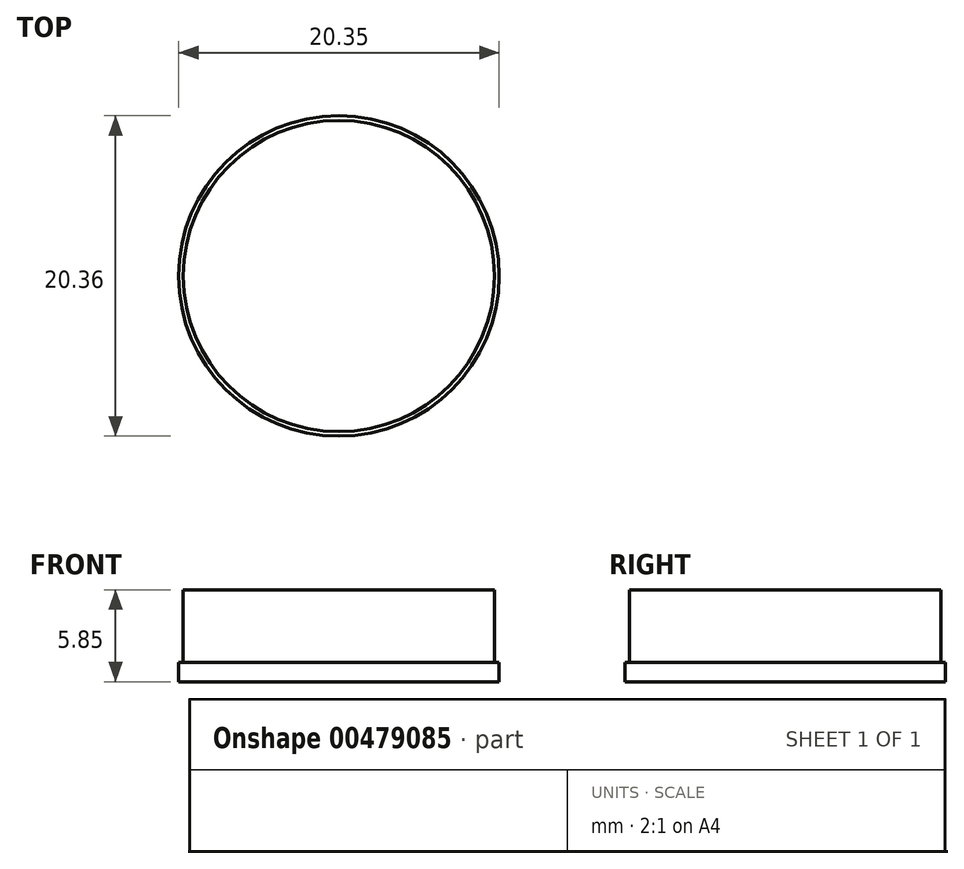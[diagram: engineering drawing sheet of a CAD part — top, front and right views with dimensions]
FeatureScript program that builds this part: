
annotation { "Feature Type Name" : "Feature", "Feature Type Description" : "" }
export const myFeature = defineFeature(function(context is Context, id is Id, definition is map)
    precondition{}
    {
        {
            var Q0;
            Q0=qCreatedBy(makeId("Front.planeOp"),FACE);
            var sketch = newSketch(context, id + "F0", { "sketchPlane" : qUnion([Q0])});
            skLineSegment(sketch, "E0", {"start": v(8.83, -3.25) * mm, "end": v(-6.17, -3.25) * mm});
            skLineSegment(sketch, "E1", {"start": v(-6.17, -3.25) * mm, "end": v(-6.17, 4.75) * mm});
            skLineSegment(sketch, "E2", {"start": v(-6.17, 4.75) * mm, "end": v(-1.18, 4.75) * mm});
            skLineSegment(sketch, "E3", {"start": v(-1.18, 4.75) * mm, "end": v(-1.18, 0.75) * mm});
            skLineSegment(sketch, "E4", {"start": v(-1.18, 0.75) * mm, "end": v(-1.48, 0.75) * mm});
            skLineSegment(sketch, "E5", {"start": v(-1.48, 0.75) * mm, "end": v(-1.48, -0.75) * mm});
            skLineSegment(sketch, "E6", {"start": v(-1.48, -0.75) * mm, "end": v(8.83, -0.75) * mm});
            skLineSegment(sketch, "E7", {"start": v(8.83, -0.75) * mm, "end": v(8.83, -3.25) * mm});
            skSolve(sketch);
        }
        {
            var Q0;
            Q0=makeQuery(id+"F0.imprint","IMPRINT",FACE,{"disambiguationData":[TD([[makeQuery(id+"F0.imprint","IMPRINT",EDGE,{"derivedFrom":sQuery(id+"F0.wireOp",EDGE,"E0")}),-1.0]])]});
            var sketch = newSketch(context, id + "F1", { "sketchPlane" : qUnion([Q0])});
            skLineSegment(sketch, "E8", {"start": v(8.83, -0.6) * mm, "end": v(-1.35, -0.6) * mm});
            skLineSegment(sketch, "E9", {"start": v(-1.35, -0.6) * mm, "end": v(-1.35, 0.64) * mm});
            skLineSegment(sketch, "E10", {"start": v(-1.35, 0.64) * mm, "end": v(-1.06, 0.64) * mm});
            skLineSegment(sketch, "E11", {"start": v(-1.06, 0.64) * mm, "end": v(-1.06, 5.26) * mm});
            skLineSegment(sketch, "E12", {"start": v(-1.06, 5.26) * mm, "end": v(8.83, 5.26) * mm});
            skLineSegment(sketch, "E13", {"start": v(8.83, 5.26) * mm, "end": v(8.83, -0.6) * mm});
            skSolve(sketch);
        }
        {
            var Q0;
            Q0=makeQuery(id+"F1.imprint","IMPRINT",FACE,{"disambiguationData":[TD([[makeQuery(id+"F1.imprint","IMPRINT",EDGE,{"derivedFrom":sQuery(id+"F1.wireOp",EDGE,"E8")}),-1.0]])]});
            var Q1;
            Q1=sQuery(id+"F1.wireOp",EDGE,"E13");
            revolve(context, id + "F2", {"entities" : qUnion([Q0]), "axis" : qUnion([Q1]), "revolveType" : RevolveType.FULL});
        }
    });
